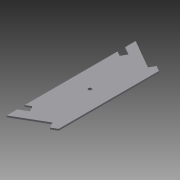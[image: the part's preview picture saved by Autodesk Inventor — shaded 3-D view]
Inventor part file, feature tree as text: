
AUTODESK INVENTOR PART (.ipt)
format: ipt  version: 2015 (Build 190159000, 159)  size: 121,856 bytes
history: native  units: in
note: dims shown in document units (in); Inventor stores cm internally (conversion verified against a paired STEP export)
features: reference x4, sketch x3, extrude x2, hole x1
ambient origin geometry x8: Origin, YZ Plane, XZ Plane, XY Plane, X Axis, Y Axis, Z Axis, Center Point
bodies: Solid1 (feature_tree)
feature tree (10):
  extrude  "Extrusion1"  TaperAngle=30.0deg  [1 undecoded]
  extrude  "Extrusion2"  Depth=0.25in TaperAngle=0.0deg
  hole  "Hole1"  [1 undecoded]
  sketch  "Sketch1"  dims[d0=120.0deg d1=30.0deg]
  sketch  "Sketch3"  dims[d2=16.0in d3=0.25in d4=0.0in]
  reference  "Reference5"
  reference  "Reference6"
  reference  "Reference7"
  reference  "Reference8"
  sketch  "Sketch4"  dims[d5=6.0in d6=0.02in d7=0.02in d8=0.02in d9=0.02in d10=0.0in d11=0.0in d12=3.0in d13=8.0in d14=0.5312in d15=0.75in d16=0.375in d17=0.25in d18=0.5635in d19=1.0in d20=0.8108in]
note: 2 required parameter values undecoded (feature->parameter linkage not recoverable at this tier; creation-order binding heuristic only, values carry confidence <= 0.55)
